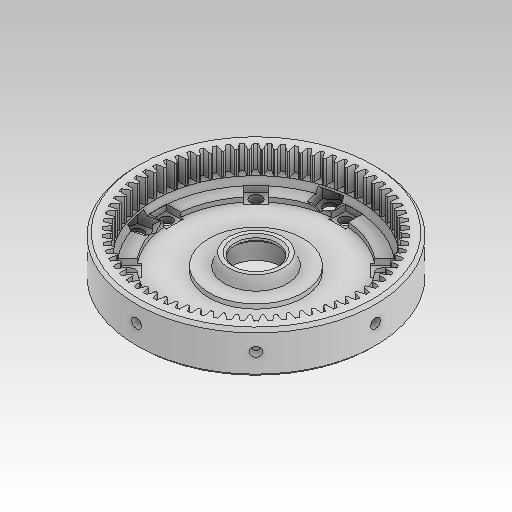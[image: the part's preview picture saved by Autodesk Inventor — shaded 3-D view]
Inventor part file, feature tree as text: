
AUTODESK INVENTOR PART (.ipt)
format: ipt  version: 2020 (Build 240168000, 168)  size: 1,848,320 bytes
history: native  units: mm
features: other x9, extrude x6, sketch x5, pattern_circular x4, chamfer x3, revolve x2, fillet x1, imported_body x1, projected_geometry x1
ambient origin geometry x8: Origin, YZ Plane, XZ Plane, XY Plane, X Axis, Y Axis, Z Axis, Center Point
bodies: Solid1 (feature_tree)
feature tree (32):
  other  "HD_mastersketch.ipt"
  other  "Blocks"
  revolve  "Revolution1"  [1 undecoded]
  extrude  "Extrusion1"  Depth=3.9mm
  extrude  "Extrusion3"  Depth=80.0mm TaperAngle=360.0deg
  pattern_circular  "Circular Pattern1"  [2 undecoded]
  extrude  "Extrusion2"  Depth=1.5mm
  fillet  "Fillet1"  Radius=700.0mm
  pattern_circular  "Circular Pattern2"  [2 undecoded]
  extrude  "Extrusion5"  Depth=1.5mm TaperAngle=0.0deg
  extrude  "Extrusion7"  Depth=1.5mm
  chamfer  "Chamfer1"  Distance=4.3mm
  extrude  "Extrusion8"  TaperAngle=0.0deg  [1 undecoded]
  chamfer  "Chamfer2"  Distance=2.268928mm
  pattern_circular  "Circular Pattern3"  [2 undecoded]
  revolve  "Revolution2"  [1 undecoded]
  pattern_circular  "Circular Pattern4"  Angle=45.0deg  [1 undecoded]
  chamfer  "Chamfer3"  Distance=8.726646mm
  other  "608 bearing"
  other  "Belt"
  other  "Rotor"
  imported_body  "Base"
  sketch  "Sketch5"  dims[d0=10.0mm d24=7.0mm d25=22.0mm d26=8.0mm]
  other  "M3NutDepth_bot"
  projected_geometry  "Projected Loop1"
  sketch  "Sketch7"  dims[d1=90.0deg d2=3.9mm]
  other  "BeltCutDepth_bot"
  sketch  "Sketch12"  dims[d4=4.0mm d5=0.0mm d6=80.0mm d7=360.0deg]
  sketch  "Sketch13"  dims[d9=0.8mm]
  sketch  "Sketch14"  dims[d11=1.8mm d12=4.0mm d13=0.0mm d14=0.45mm d15=700.0mm d16=360.0deg d18=5.7mm d19=4.0mm d20=0.0mm d29=47.0mm d30=4.3mm d31=0.0mm d32=0.0mm d38=2.268928mm d39=7.2mm d40=1.5mm d41=3.2mm d42=0.0mm d43=0.0mm d44=2.0mm d45=2.0mm d46=45.0deg d47=8.726646mm d48=0.523599mm d49=0.523599mm d50=0.523599mm d51=0.523599mm d52=0.523599mm d53=0.523599mm d56=2.792527mm d57=0.523599mm d58=68.0mm d59=70.740362mm d60=1.780032mm d61=9.749343mm d62=7.969311mm d63=6.189278mm d64=4.409246mm d65=2.629213mm d66=0.523599mm d67=0.523599mm d68=0.523599mm d69=0.523599mm d70=0.523599mm d72=11.529376mm d73=13.309408mm d74=15.089441mm d75=16.869473mm d76=18.649506mm d77=0.523599mm d78=0.523599mm d79=20.429538mm d80=22.209571mm d82=0.250579mm d83=72.932651mm d84=22.5mm d85=15.0mm d86=2.0mm d87=1.0mm d88=0.0mm d89=0.3mm d90=1.0mm d91=45.0deg d92=80.0mm d93=360.0deg d97=7.5mm d98=1.6mm d99=1.4mm d100=2.5mm d101=1.0mm d102=90.0deg d103=80.0mm d104=360.0deg d106=0.75mm d107=2.0mm d108=45.0deg]
  other  "608 bearing:1"
  other  "608 bearing:2"
note: 10 required parameter values undecoded (feature->parameter linkage not recoverable at this tier; creation-order binding heuristic only, values carry confidence <= 0.55)